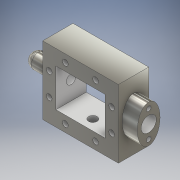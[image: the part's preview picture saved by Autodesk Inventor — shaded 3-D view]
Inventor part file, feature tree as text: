
AUTODESK INVENTOR PART (.ipt)
format: ipt  version: 2017 (Build 210142000, 142)  size: 237,056 bytes
history: native  units: mm
features: extrude x8, sketch x5, fillet x1
ambient origin geometry x8: Origin, YZ Plane, XZ Plane, XY Plane, X Axis, Y Axis, Z Axis, Center Point
bodies: Solid1 (feature_tree)
feature tree (14):
  extrude  "Extrusion1"  Depth=36.0mm TaperAngle=0.0deg
  sketch  "Sketch2"  dims[d5=8.0mm d6=20.0mm d7=6.0mm d8=12.0mm]
  extrude  "Extrusion3"  Depth=6.0mm TaperAngle=0.0deg
  extrude  "Extrusion4"  Depth=8.0mm TaperAngle=0.0deg
  extrude  "Extrusion5"  Depth=8.0mm TaperAngle=0.0deg
  extrude  "Extrusion6"  Depth=10.0mm
  extrude  "Extrusion7"  Depth=4.0mm
  extrude  "Extrusion9"  Depth=10.0mm
  fillet  "Fillet1"  Radius=36.0mm
  extrude  "Extrusion11"  Depth=10.0mm
  sketch  "Sketch1"  dims[d0=40.0mm d1=36.0mm d2=26.0mm d3=16.0mm d4=0.0mm]
  sketch  "Sketch3"  dims[d9=3.0mm d10=14.0mm d11=2.5mm d12=2.5mm d13=5.0mm d16=6.0mm d17=0.0mm]
  sketch  "Sketch4"  dims[d18=8.0mm d19=40.0mm d20=0.0mm]
  sketch  "Sketch6"  dims[d21=8.0mm d22=0.0mm d23=8.0mm d24=0.0mm d25=6.0mm d26=12.0mm d27=5.0mm d28=3.0mm d29=3.0mm d30=3.0mm d31=3.0mm d32=90.0deg d33=32.0mm d34=4.0mm d35=18.0mm d36=36.0mm d37=13.0mm d38=16.5mm d39=36.0mm d40=20.0mm d41=20.0mm d42=20.0mm d43=8.0mm d44=20.5mm d45=16.0mm d46=0.0mm d47=10.0mm d48=6.0mm d49=21.25mm d50=28.0mm d51=0.0mm d52=0.0mm d53=0.0mm d54=28.0mm d55=8.0mm d56=8.0mm d57=1.75mm d58=15.75mm d59=8.0mm d60=8.0mm d61=28.0mm d62=8.0mm d63=8.0mm d66=14.0mm d67=0.0mm d68=4.0mm d73=4.5mm d74=21.0mm d75=10.0mm d76=0.0mm]
